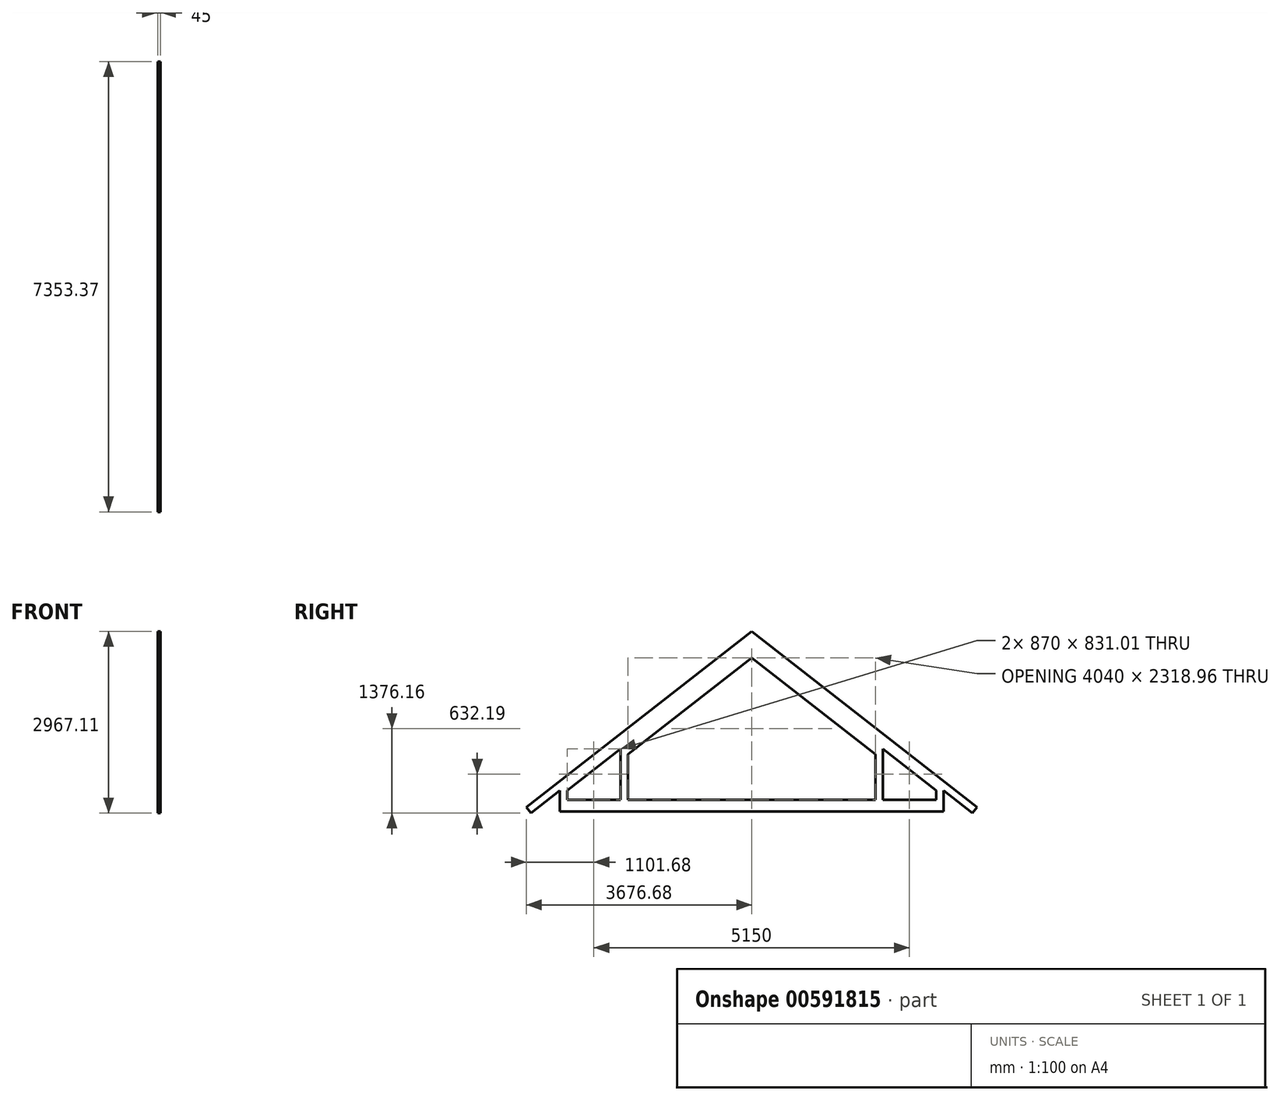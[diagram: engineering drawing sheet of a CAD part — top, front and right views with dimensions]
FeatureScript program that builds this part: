
annotation { "Feature Type Name" : "Feature", "Feature Type Description" : "" }
export const myFeature = defineFeature(function(context is Context, id is Id, definition is map)
    precondition{}
    {
        {
            var Q0;
            Q0=qCreatedBy(makeId("Right.planeOp"),FACE);
            var sketch = newSketch(context, id + "F0", { "sketchPlane" : qUnion([Q0])});
            skLineSegment(sketch, "E0", {"start": v(-3120, 2101.32) * mm, "end": v(-3120, 2589.9) * mm});
            skLineSegment(sketch, "E1", {"start": v(-6240, 0) * mm, "end": v(-3120, 2437.61) * mm});
            skLineSegment(sketch, "E2", {"start": v(-3120, 2437.61) * mm, "end": v(0, 0) * mm});
            skLineSegment(sketch, "E3", {"start": v(-3120, 2589.9) * mm, "end": v(-6707.88, -213.27) * mm});
            skLineSegment(sketch, "E4", {"start": v(-3120, 2589.9) * mm, "end": v(467.88, -213.27) * mm});
            skLineSegment(sketch, "E5.0", {"start": v(-3120, 2101.32) * mm, "end": v(-1222.76, 619.04) * mm});
            skLineSegment(sketch, "E6", {"start": v(-1222.76, 619.04) * mm, "end": v(-1222.76, -172.9) * mm});
            skLineSegment(sketch, "E7", {"start": v(-5017.24, 619.04) * mm, "end": v(-5017.24, -172.9) * mm});
            skLineSegment(sketch, "E8.trimOffspring", {"start": v(-5017.24, 619.04) * mm, "end": v(-3120, 2101.32) * mm});
            skPoint(sketch, "E9.orphan", {"position": v(-3120, 0) * mm});
            skLineSegment(sketch, "E10.0", {"start": v(-3120, 2285.33) * mm, "end": v(-194.91, 0) * mm});
            skLineSegment(sketch, "E10.1", {"start": v(-6045.09, 0) * mm, "end": v(-3120, 2285.33) * mm});
            skLineSegment(sketch, "E11", {"start": v(-6240, 0) * mm, "end": v(-6045.09, 0) * mm});
            skLineSegment(sketch, "E12", {"start": v(0, 0) * mm, "end": v(-194.91, 0) * mm});
            skLineSegment(sketch, "E13", {"start": v(-1222.76, 619.04) * mm, "end": v(-1222.76, 803.04) * mm});
            skLineSegment(sketch, "E14", {"start": v(-5017.24, 619.04) * mm, "end": v(-5017.24, 803.04) * mm});
            skLineSegment(sketch, "E15.0", {"start": v(-5137.24, 600) * mm, "end": v(-5137.24, -172.9) * mm});
            skLineSegment(sketch, "E15.1", {"start": v(-5137.24, 600) * mm, "end": v(-5137.24, 709.29) * mm});
            skLineSegment(sketch, "E16.0", {"start": v(-1102.76, 600) * mm, "end": v(-1102.76, 709.29) * mm});
            skLineSegment(sketch, "E16.1", {"start": v(-1102.76, 600) * mm, "end": v(-1102.76, -172.9) * mm});
            skLineSegment(sketch, "E17", {"start": v(-1222.76, -400) * mm, "end": v(-1102.76, -400) * mm});
            skLineSegment(sketch, "E18", {"start": v(-5017.24, -342.9) * mm, "end": v(-5137.24, -342.9) * mm});
            skLineSegment(sketch, "E19", {"start": v(-6240, 0) * mm, "end": v(-6634, -307.83) * mm});
            skLineSegment(sketch, "E20", {"start": v(-6634, -307.83) * mm, "end": v(-6707.88, -213.27) * mm});
            skLineSegment(sketch, "E21", {"start": v(0, 0) * mm, "end": v(394, -307.83) * mm});
            skLineSegment(sketch, "E22", {"start": v(394, -307.83) * mm, "end": v(467.88, -213.27) * mm});
            skLineSegment(sketch, "E23", {"start": v(-6240, 0) * mm, "end": v(-6240, -342.9) * mm});
            skLineSegment(sketch, "E24", {"start": v(-6240, -342.9) * mm, "end": v(0, -342.9) * mm});
            skLineSegment(sketch, "E25", {"start": v(0, 0) * mm, "end": v(0, -342.9) * mm});
            skLineSegment(sketch, "E26.0", {"start": v(-6120, 0) * mm, "end": v(-6120, -172.9) * mm});
            skLineSegment(sketch, "E26.2", {"start": v(-120, 0) * mm, "end": v(-120, -172.9) * mm});
            skLineSegment(sketch, "E27.0", {"start": v(-6120, -172.9) * mm, "end": v(-5137.24, -172.9) * mm});
            skLineSegment(sketch, "E28.trimOffspring", {"start": v(-5017.24, -172.9) * mm, "end": v(-1222.76, -172.9) * mm});
            skLineSegment(sketch, "E29.trimOffspring", {"start": v(-1102.76, -172.9) * mm, "end": v(-120, -172.9) * mm});
            skLineSegment(sketch, "E30", {"start": v(6514.65, -342.9) * mm, "end": v(6514.65, 257.1) * mm});
            skLineSegment(sketch, "E31", {"start": v(6514.65, 257.1) * mm, "end": v(6038.7, -114.77) * mm});
            skLineSegment(sketch, "E32", {"start": v(6038.7, -114.77) * mm, "end": v(6094.1, -185.69) * mm});
            skLineSegment(sketch, "E33", {"start": v(6094.1, -185.69) * mm, "end": v(6514.65, 9.63) * mm});
            skLineSegment(sketch, "E34", {"start": v(6514.65, -342.9) * mm, "end": v(9634.65, -342.9) * mm});
            skLineSegment(sketch, "E35", {"start": v(9634.65, -342.9) * mm, "end": v(9634.65, 2695.1) * mm});
            skLineSegment(sketch, "E36", {"start": v(9634.65, 2695.1) * mm, "end": v(6514.65, 257.1) * mm});
            skLineSegment(sketch, "E37", {"start": v(6514.65, 9.63) * mm, "end": v(9634.65, 2447.24) * mm});
            skLineSegment(sketch, "E38", {"start": v(6514.65, -342.9) * mm, "end": v(6514.65, -147.9) * mm});
            skLineSegment(sketch, "E39", {"start": v(6514.65, -147.9) * mm, "end": v(9634.65, -147.9) * mm});
            skLineSegment(sketch, "E40", {"start": v(6514.65, -147.9) * mm, "end": v(6634.65, -147.9) * mm});
            skLineSegment(sketch, "E41", {"start": v(6634.65, -147.9) * mm, "end": v(6634.65, 103.39) * mm});
            skLineSegment(sketch, "E42", {"start": v(9634.65, -147.9) * mm, "end": v(7614.65, -147.9) * mm});
            skLineSegment(sketch, "E43", {"start": v(7614.65, -147.9) * mm, "end": v(7614.65, 869.05) * mm});
            skLineSegment(sketch, "E44", {"start": v(7614.65, 700.4) * mm, "end": v(9634.65, 2278.85) * mm});
            skLineSegment(sketch, "E45", {"start": v(7463.7, 751.1) * mm, "end": v(7463.7, -147.9) * mm});
            skLineSegment(sketch, "E46.MirrorCS", {"start": v(12754.65, -342.9) * mm, "end": v(12754.65, -147.9) * mm});
            skLineSegment(sketch, "E47.MirrorCS", {"start": v(13230.61, -114.77) * mm, "end": v(13175.2, -185.69) * mm});
            skLineSegment(sketch, "E48.MirrorCS", {"start": v(12754.65, -147.9) * mm, "end": v(12634.65, -147.9) * mm});
            skLineSegment(sketch, "E49.MirrorCS", {"start": v(12634.65, -147.9) * mm, "end": v(12634.65, 103.39) * mm});
            skLineSegment(sketch, "E50.MirrorCS", {"start": v(13175.2, -185.69) * mm, "end": v(12754.65, 9.63) * mm});
            skLineSegment(sketch, "E51.MirrorCS", {"start": v(12754.65, -342.9) * mm, "end": v(12754.65, 257.1) * mm});
            skLineSegment(sketch, "E52.MirrorCS", {"start": v(12754.65, 257.1) * mm, "end": v(13230.61, -114.77) * mm});
            skLineSegment(sketch, "E53.MirrorCS", {"start": v(12754.65, -342.9) * mm, "end": v(9634.65, -342.9) * mm});
            skLineSegment(sketch, "E54.MirrorCS", {"start": v(12754.65, -147.9) * mm, "end": v(9634.65, -147.9) * mm});
            skLineSegment(sketch, "E55.MirrorCS", {"start": v(9634.65, 2695.1) * mm, "end": v(12754.65, 257.1) * mm});
            skLineSegment(sketch, "E56.MirrorCS", {"start": v(11654.65, -147.9) * mm, "end": v(11654.65, 869.05) * mm});
            skLineSegment(sketch, "E57.MirrorCS", {"start": v(11805.62, 751.1) * mm, "end": v(11805.62, -147.9) * mm});
            skLineSegment(sketch, "E58.MirrorCS", {"start": v(9634.65, -147.9) * mm, "end": v(11654.65, -147.9) * mm});
            skLineSegment(sketch, "E59.MirrorCS", {"start": v(11654.65, 700.4) * mm, "end": v(9634.65, 2278.85) * mm});
            skLineSegment(sketch, "E60.MirrorCS", {"start": v(12754.65, 9.63) * mm, "end": v(9634.65, 2447.24) * mm});
            skLineSegment(sketch, "E61", {"start": v(0, -342.9) * mm, "end": v(0, 152.28) * mm});
            skLineSegment(sketch, "E62", {"start": v(3942.63, -4776.5) * mm, "end": v(7072.63, -4776.5) * mm});
            skLineSegment(sketch, "E63", {"start": v(7072.63, -4776.5) * mm, "end": v(7072.63, -4581.5) * mm});
            skLineSegment(sketch, "E64", {"start": v(3942.63, -4776.5) * mm, "end": v(3942.63, -4428.79) * mm});
            skLineSegment(sketch, "E65", {"start": v(3942.63, -4276.5) * mm, "end": v(3395.95, -4703.62) * mm});
            skLineSegment(sketch, "E66", {"start": v(3395.95, -4703.62) * mm, "end": v(3469.83, -4798.19) * mm});
            skLineSegment(sketch, "E67", {"start": v(3469.83, -4798.19) * mm, "end": v(3942.63, -4428.79) * mm});
            skLineSegment(sketch, "E68", {"start": v(3942.63, -4776.5) * mm, "end": v(3942.63, -4581.5) * mm});
            skLineSegment(sketch, "E69", {"start": v(3942.63, -4581.5) * mm, "end": v(7072.63, -4581.5) * mm});
            skLineSegment(sketch, "E70", {"start": v(3942.63, -4276.5) * mm, "end": v(7072.63, -1831.08) * mm});
            skLineSegment(sketch, "E71.0", {"start": v(4062.69, -4430.17) * mm, "end": v(7072.63, -2078.54) * mm});
            skLineSegment(sketch, "E72", {"start": v(4062.69, -4430.17) * mm, "end": v(4062.63, -4430.21) * mm});
            skLineSegment(sketch, "E73.0", {"start": v(4062.63, -4581.5) * mm, "end": v(4062.63, -4430.21) * mm});
            skLineSegment(sketch, "E74", {"start": v(3942.63, -4428.79) * mm, "end": v(4064.45, -4428.79) * mm});
            skLineSegment(sketch, "E75.trimOffspring", {"start": v(7072.63, -2078.54) * mm, "end": v(7072.63, -1831.08) * mm});
            skLineSegment(sketch, "E76", {"start": v(7072.63, -4776.5) * mm, "end": v(7072.63, -773.27) * mm});
            skLineSegment(sketch, "E77.0", {"start": v(5052.63, -3840.75) * mm, "end": v(7072.63, -2262.55) * mm});
            skLineSegment(sketch, "E78", {"start": v(7072.63, -4581.5) * mm, "end": v(5052.63, -4581.5) * mm});
            skLineSegment(sketch, "E79", {"start": v(5052.63, -4581.5) * mm, "end": v(5052.63, -3656.74) * mm});
            skLineSegment(sketch, "E80.0", {"start": v(4932.63, -4581.5) * mm, "end": v(4932.63, -3750.5) * mm});
            skLineSegment(sketch, "E81.MirrorCS", {"start": v(10082.58, -4430.17) * mm, "end": v(10082.63, -4430.21) * mm});
            skLineSegment(sketch, "E82.MirrorCS", {"start": v(10082.63, -4581.5) * mm, "end": v(10082.63, -4430.21) * mm});
            skLineSegment(sketch, "E83.MirrorCS", {"start": v(10202.63, -4428.79) * mm, "end": v(10080.81, -4428.79) * mm});
            skLineSegment(sketch, "E84.MirrorCS", {"start": v(10202.63, -4776.5) * mm, "end": v(10202.63, -4581.5) * mm});
            skLineSegment(sketch, "E85.MirrorCS", {"start": v(10202.63, -4776.5) * mm, "end": v(10202.63, -4428.79) * mm});
            skLineSegment(sketch, "E86.MirrorCS", {"start": v(10749.32, -4703.62) * mm, "end": v(10675.44, -4798.19) * mm});
            skLineSegment(sketch, "E87.MirrorCS", {"start": v(10675.44, -4798.19) * mm, "end": v(10202.63, -4428.79) * mm});
            skLineSegment(sketch, "E88.MirrorCS", {"start": v(9212.63, -4581.5) * mm, "end": v(9212.63, -3750.5) * mm});
            skLineSegment(sketch, "E89.MirrorCS", {"start": v(10202.63, -4581.5) * mm, "end": v(7072.63, -4581.5) * mm});
            skLineSegment(sketch, "E90.MirrorCS", {"start": v(10202.63, -4276.5) * mm, "end": v(10749.32, -4703.62) * mm});
            skLineSegment(sketch, "E91.MirrorCS", {"start": v(9092.63, -4581.5) * mm, "end": v(9092.63, -3656.74) * mm});
            skLineSegment(sketch, "E92.MirrorCS", {"start": v(7072.63, -4581.5) * mm, "end": v(9092.63, -4581.5) * mm});
            skLineSegment(sketch, "E93.MirrorCS", {"start": v(10082.58, -4430.17) * mm, "end": v(7072.63, -2078.54) * mm});
            skLineSegment(sketch, "E94.MirrorCS", {"start": v(10202.63, -4776.5) * mm, "end": v(7072.63, -4776.5) * mm});
            skLineSegment(sketch, "E95.MirrorCS", {"start": v(9092.63, -3840.75) * mm, "end": v(7072.63, -2262.55) * mm});
            skLineSegment(sketch, "E96.MirrorCS", {"start": v(10202.63, -4276.5) * mm, "end": v(7072.63, -1831.08) * mm});
            skSolve(sketch);
        }
        {
            var Q0;
            {var subQ4=sQuery(id+"F0.wireOp",EDGE,"E83.MirrorCS");Q0=makeQuery(id+"F0.imprint","IMPRINT",FACE,{"disambiguationData":[TD([[makeQuery(id+"F0.imprint","IMPRINT",EDGE,{"derivedFrom":subQ4}),-1.0]])]});}
            var Q1;
            {var subQ3=sQuery(id+"F0.wireOp",EDGE,"E95.MirrorCS");Q1=makeQuery(id+"F0.imprint","IMPRINT",FACE,{"disambiguationData":[TD([[makeQuery(id+"F0.imprint","IMPRINT",EDGE,{"derivedFrom":subQ3}),-1.0]])]});}
            var Q2;
            Q2=makeQuery(id+"F0.imprint","IMPRINT",FACE,{"disambiguationData":[TD([[makeQuery(id+"F0.imprint","IMPRINT",EDGE,{"derivedFrom":sQuery(id+"F0.wireOp",EDGE,"E65")}),1.0]])]});
            var Q3;
            {var subQ5=sQuery(id+"F0.wireOp",EDGE,"E77.0");Q3=makeQuery(id+"F0.imprint","IMPRINT",FACE,{"disambiguationData":[TD([[makeQuery(id+"F0.imprint","IMPRINT",EDGE,{"derivedFrom":subQ5}),1.0]])]});}
            var Q4;
            {var subQ6=sQuery(id+"F0.wireOp",EDGE,"E80.0");Q4=makeQuery(id+"F0.imprint","IMPRINT",FACE,{"disambiguationData":[TD([[makeQuery(id+"F0.imprint","IMPRINT",EDGE,{"derivedFrom":subQ6}),-1.0]])]});}
            var Q5;
            {var subQ4=sQuery(id+"F0.wireOp",EDGE,"E64");Q5=makeQuery(id+"F0.imprint","IMPRINT",FACE,{"disambiguationData":[TD([[makeQuery(id+"F0.imprint","IMPRINT",EDGE,{"derivedFrom":subQ4}),-1.0]])]});}
            var Q6;
            Q6=makeQuery(id+"F0.imprint","IMPRINT",FACE,{"disambiguationData":[TD([[makeQuery(id+"F0.imprint","IMPRINT",EDGE,{"derivedFrom":sQuery(id+"F0.wireOp",EDGE,"E62")}),1.0]])]});
            var Q7;
            Q7=makeQuery(id+"F0.imprint","IMPRINT",FACE,{"disambiguationData":[TD([[makeQuery(id+"F0.imprint","IMPRINT",EDGE,{"derivedFrom":sQuery(id+"F0.wireOp",EDGE,"E63")}),-1.0]])]});
            var Q8;
            {var subQ5=sQuery(id+"F0.wireOp",EDGE,"E88.MirrorCS");Q8=makeQuery(id+"F0.imprint","IMPRINT",FACE,{"disambiguationData":[TD([[makeQuery(id+"F0.imprint","IMPRINT",EDGE,{"derivedFrom":subQ5}),1.0]])]});}
            var Q9;
            {var subQ5=sQuery(id+"F0.wireOp",EDGE,"E81.MirrorCS");Q9=makeQuery(id+"F0.imprint","IMPRINT",FACE,{"disambiguationData":[TD([[makeQuery(id+"F0.imprint","IMPRINT",EDGE,{"derivedFrom":subQ5}),1.0]])]});}
            extrude(context, id + "F1", {"entities" : qUnion([Q0, Q1, Q2, Q3, Q4, Q5, Q6, Q7, Q8, Q9]), "depth" : 45 * mm, "offsetDistance" : 25 * mm});
        }
    });
